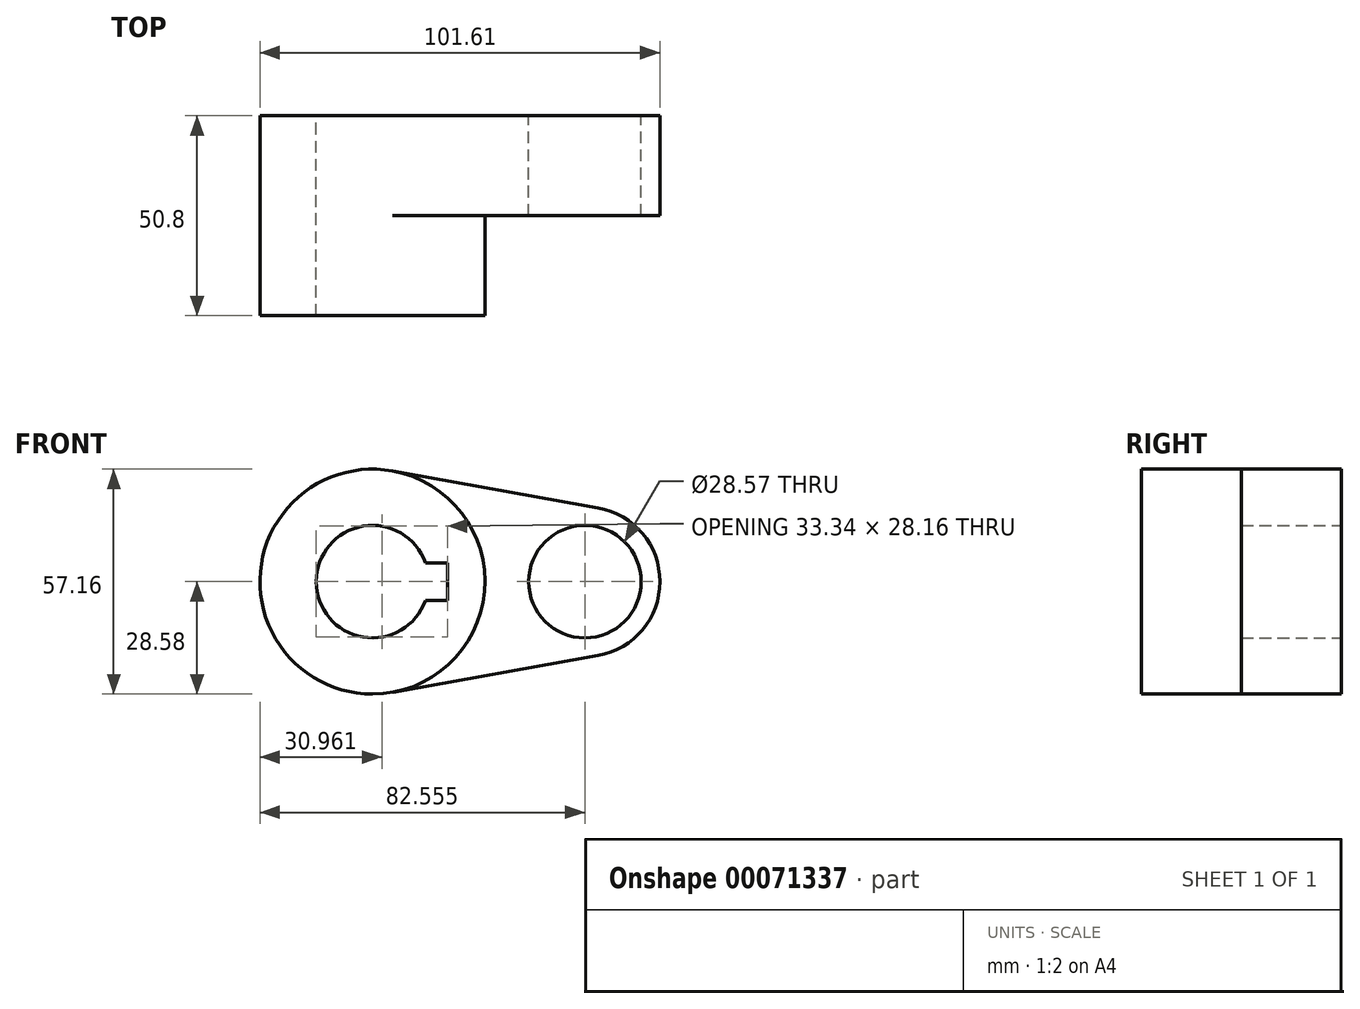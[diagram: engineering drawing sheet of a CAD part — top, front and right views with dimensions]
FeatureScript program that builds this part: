
annotation { "Feature Type Name" : "Feature", "Feature Type Description" : "" }
export const myFeature = defineFeature(function(context is Context, id is Id, definition is map)
    precondition{}
    {
        {
            var Q0;
            Q0=qCreatedBy(makeId("Front.planeOp"),FACE);
            var sketch = newSketch(context, id + "F0", { "sketchPlane" : qUnion([Q0])});
            skCircle(sketch, "E0", {"center": v(0, 0) * mm, "radius": 28.57 * mm});
            skCircle(sketch, "E1", {"center": v(53.98, 0) * mm, "radius": 19.05 * mm});
            skLineSegment(sketch, "E2", {"start": v(5.04, 28.13) * mm, "end": v(57.34, 18.75) * mm});
            skLineSegment(sketch, "E3", {"start": v(5.04, -28.13) * mm, "end": v(57.34, -18.75) * mm});
            skCircle(sketch, "E4", {"center": v(0, 0) * mm, "radius": 14.29 * mm});
            skCircle(sketch, "E5", {"center": v(53.98, 0) * mm, "radius": 14.29 * mm});
            skLineSegment(sketch, "E6.rect.bottom", {"start": v(19.05, -4.76) * mm, "end": v(-19.05, -4.76) * mm});
            skLineSegment(sketch, "E6.rect.top", {"start": v(19.05, 4.76) * mm, "end": v(-19.05, 4.76) * mm});
            skLineSegment(sketch, "E6.rect.left", {"start": v(19.05, -4.76) * mm, "end": v(19.05, 4.76) * mm});
            skLineSegment(sketch, "E6.rect.right", {"start": v(-19.05, -4.76) * mm, "end": v(-19.05, 4.76) * mm});
            skSolve(sketch);
        }
        {
            var Q0;
            {var subQ0=sQuery(id+"F0.wireOp",EDGE,"E2");Q0=makeQuery(id+"F0.imprint","IMPRINT",FACE,{"disambiguationData":[TD([[makeQuery(id+"F0.imprint","IMPRINT",EDGE,{"derivedFrom":subQ0}),-1.0]])]});}
            var Q1;
            Q1=makeQuery(id+"F0.imprint","IMPRINT",FACE,{"disambiguationData":[TD([[makeQuery(id+"F0.imprint","IMPRINT",EDGE,{"derivedFrom":sQuery(id+"F0.wireOp",EDGE,"E5")}),-1.0]])]});
            extrude(context, id + "F1", {"entities" : qUnion([Q0, Q1]), "depth" : 25.4 * mm});
        }
        {
            var Q0;
            {var subQ11=sQuery(id+"F0.wireOp",EDGE,"E6.rect.left");Q0=makeQuery(id+"F0.imprint","IMPRINT",FACE,{"disambiguationData":[TD([[makeQuery(id+"F0.imprint","IMPRINT",EDGE,{"derivedFrom":subQ11}),-1.0]])]});}
            var Q1;
            {var subQ5=sQuery(id+"F0.wireOp",EDGE,"E6.rect.right");Q1=makeQuery(id+"F0.imprint","IMPRINT",FACE,{"disambiguationData":[TD([[makeQuery(id+"F0.imprint","IMPRINT",EDGE,{"derivedFrom":subQ5}),-1.0]])]});}
            extrude(context, id + "F2", {"entities" : qUnion([Q0, Q1]), "operationType" : NewBodyOperationType.ADD, "depth" : 50.8 * mm});
        }
    });
